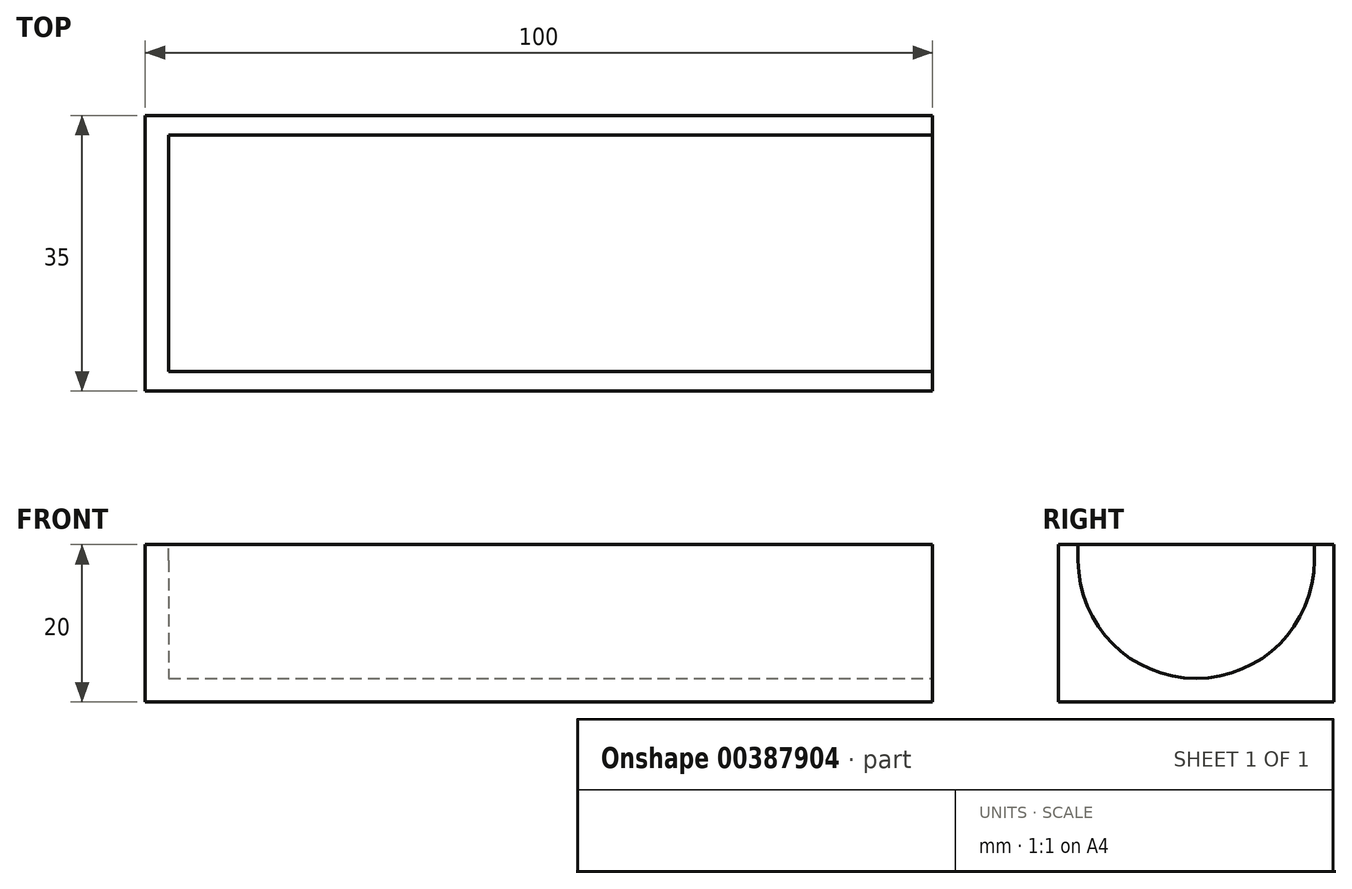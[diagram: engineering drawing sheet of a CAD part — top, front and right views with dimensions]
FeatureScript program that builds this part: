
annotation { "Feature Type Name" : "Feature", "Feature Type Description" : "" }
export const myFeature = defineFeature(function(context is Context, id is Id, definition is map)
    precondition{}
    {
        {
            var Q0;
            Q0=qCreatedBy(makeId("Top.planeOp"),FACE);
            var sketch = newSketch(context, id + "F0", { "sketchPlane" : qUnion([Q0])});
            skLineSegment(sketch, "E0.bottom", {"start": v(-50, 17.5) * mm, "end": v(50, 17.5) * mm});
            skLineSegment(sketch, "E0.top", {"start": v(-50, -17.5) * mm, "end": v(50, -17.5) * mm});
            skLineSegment(sketch, "E0.left", {"start": v(-50, 17.5) * mm, "end": v(-50, -17.5) * mm});
            skLineSegment(sketch, "E0.right", {"start": v(50, 17.5) * mm, "end": v(50, -17.5) * mm});
            skLineSegment(sketch, "E1", {"start": v(0, 67.4) * mm, "end": v(0, -104.1) * mm});
            skLineSegment(sketch, "E2", {"start": v(-206.91, 0) * mm, "end": v(255.53, 0) * mm});
            skSolve(sketch);
        }
        {
            var Q0;
            Q0 = qSketchRegion(id + "F0", true);
            extrude(context, id + "F1", {"entities" : qUnion([Q0]), "depth" : 20 * mm});
        }
        {
            var Q0;
            Q0=makeQuery(id+"F1.opExtrude","SWEPT_FACE",FACE,{"disambiguationData":[OSD([sQuery(id+"F0.wireOp",EDGE,"E0.right")])]});
            var sketch = newSketch(context, id + "F2", { "sketchPlane" : qUnion([Q0])});
            skArc(sketch, "E3", {"start": v(15, 18) * mm, "mid": v(0, 3) * mm, "end": v(-15, 18) * mm});
            skLineSegment(sketch, "E4", {"start": v(-15, 18) * mm, "end": v(-15, 20) * mm});
            skLineSegment(sketch, "E5", {"start": v(15, 18) * mm, "end": v(15, 20) * mm});
            skLineSegment(sketch, "E6", {"start": v(15, 20) * mm, "end": v(-15, 20) * mm});
            skSolve(sketch);
        }
        {
            var Q0;
            Q0 = qSketchRegion(id + "F2", true);
            extrude(context, id + "F3", {"entities" : qUnion([Q0]), "operationType" : NewBodyOperationType.REMOVE, "oppositeDirection" : true, "depth" : 97 * mm});
        }
    });
